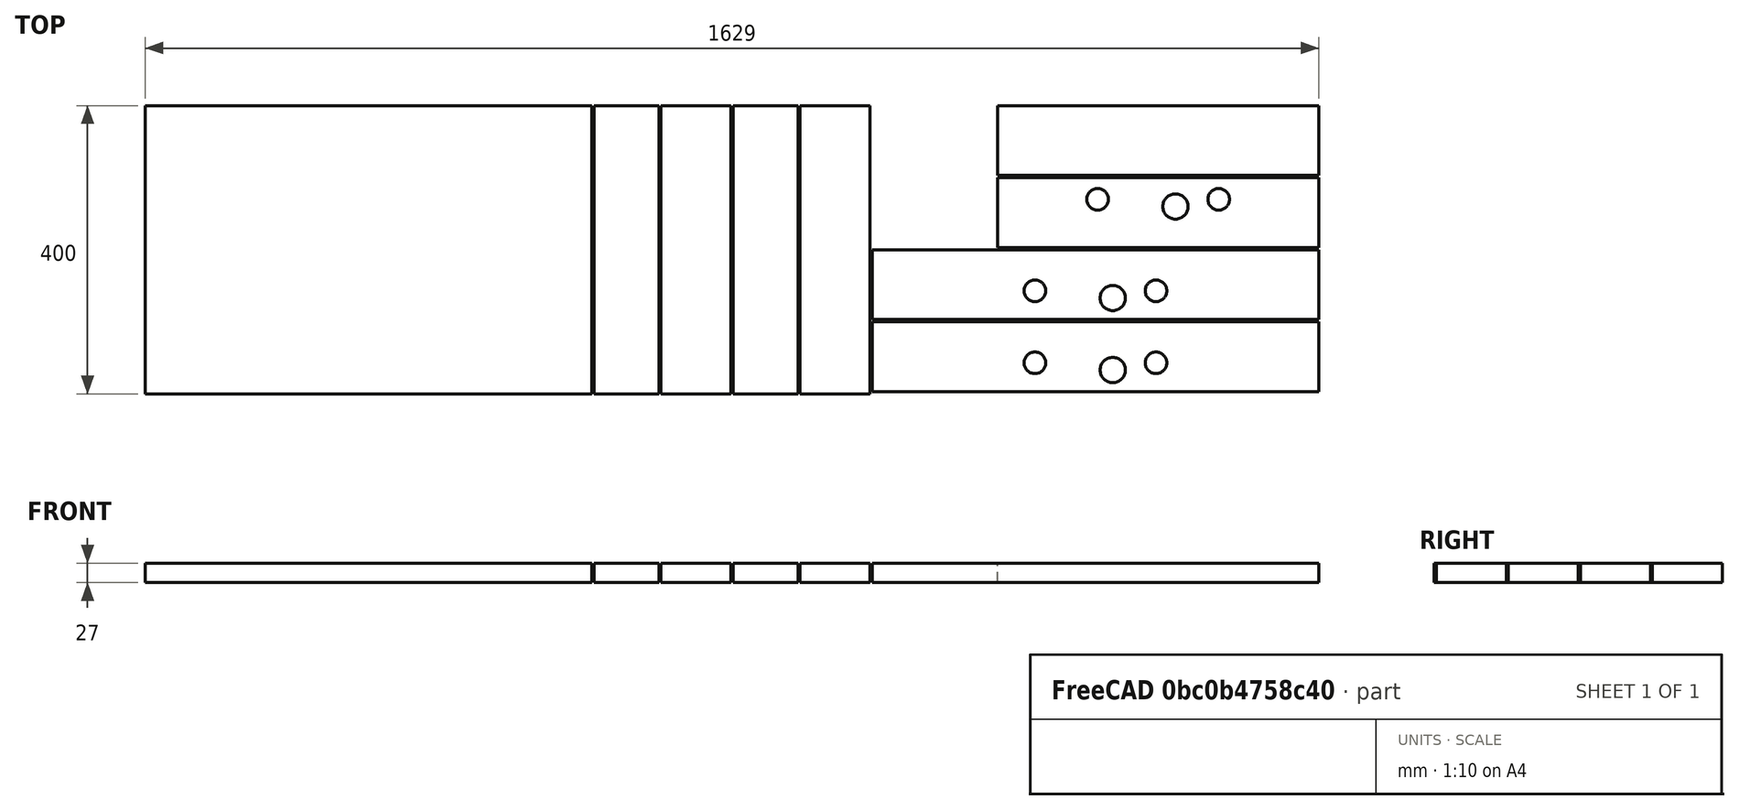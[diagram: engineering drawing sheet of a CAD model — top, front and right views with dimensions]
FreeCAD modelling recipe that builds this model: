
FCSTD DOCUMENT  (FreeCAD 0.20R25131 (Git))
Label: Zuschnitt
License: All rights reserved
LicenseURL: http://en.wikipedia.org/wiki/All_rights_reserved
objects: App::FeaturePython×70, Part::FeaturePython×41, App::Link×6, App::LinkElement×6, App::MeasureDistance×2
note: 40 computed .brp shape members not serialized (recipe doc carries the construction recipe); baked Part::Feature solids carry a one-line shape summary decoded from their .brp
EXTERNAL_REF file=Arbeitsfläche.FCStd obj=Assembly
EXTERNAL_REF file=Innen_hinten.FCStd obj=Assembly
EXTERNAL_REF file=Innen_vorne.FCStd obj=Assembly
EXTERNAL_REF file=Seitenteil.FCStd obj=Assembly
EXTERNAL_REF file=Zange.FCStd obj=Assembly
EXTERNAL_REF file=Klemmfläche.FCStd obj=Assembly

FEATURE [App::Link] Link  label="Arbeitsfläche"
  LinkedObject = -> <external Arbeitsfläche.FCStd>#Assembly
FEATURE [App::Link] Link001  label="Innen_hinten"
  LinkPlacement = pos=(1183,303,-4.4127e-12) rot=(0,0,1;0rad)
  LinkedObject = -> <external Innen_hinten.FCStd>#Assembly
  Placement = pos=(1183,303,-4.4127e-12) rot=(0,0,1;0rad)
FEATURE [App::Link] Link002  label="Innen_vorne"
  LinkPlacement = pos=(1406,203,-7.3976e-12) rot=(0,0,1;0rad)
  LinkedObject = -> <external Innen_vorne.FCStd>#Assembly
  Placement = pos=(1406,203,-7.3976e-12) rot=(0,0,1;0rad)
FEATURE [App::LinkElement] Link003_i0
  LinkPlacement = pos=(909,-4.7251e-12,-4.838e-13) rot=(0,0,1;0rad)
  LinkedObject = -> <external Seitenteil.FCStd>#Assembly
  Placement = pos=(909,-4.7251e-12,-4.838e-13) rot=(0,0,1;0rad)
FEATURE [App::LinkElement] Link003_i1
  LinkPlacement = pos=(813,400,4.313e-13) rot=(0,0,-1;3.14159rad)
  LinkedObject = -> <external Seitenteil.FCStd>#Assembly
  Placement = pos=(813,400,4.313e-13) rot=(0,0,-1;3.14159rad)
FEATURE [App::Link] Link003  label="Seitenteil"
  ElementCount = 2
  ElementList = -> [Link003_i0,Link003_i1]
  LinkedObject = -> <external Seitenteil.FCStd>#Assembly
FEATURE [App::LinkElement] Link004_i0
  LinkPlacement = pos=(1319,103,-6.2994e-12) rot=(0,0,1;0rad)
  LinkedObject = -> <external Zange.FCStd>#Assembly
  Placement = pos=(1319,103,-6.2994e-12) rot=(0,0,1;0rad)
FEATURE [App::LinkElement] Link004_i1
  LinkPlacement = pos=(1319,3,-6.3593e-12) rot=(0,0,1;0rad)
  LinkedObject = -> <external Zange.FCStd>#Assembly
  Placement = pos=(1319,3,-6.3593e-12) rot=(0,0,1;0rad)
FEATURE [App::Link] Link004  label="Zange"
  ElementCount = 2
  ElementList = -> [Link004_i0,Link004_i1]
  LinkedObject = -> <external Zange.FCStd>#Assembly
FEATURE [App::LinkElement] Link005_i0
  LinkPlacement = pos=(623,4.9e-15,2.005e-13) rot=(0,0,1;0rad)
  LinkedObject = -> <external Klemmfläche.FCStd>#Assembly
  Placement = pos=(623,4.9e-15,2.005e-13) rot=(0,0,1;0rad)
FEATURE [App::LinkElement] Link005_i1
  LinkPlacement = pos=(816,-4.5613e-12,-6.54e-14) rot=(0,0,1;0rad)
  LinkedObject = -> <external Klemmfläche.FCStd>#Assembly
  Placement = pos=(816,-4.5613e-12,-6.54e-14) rot=(0,0,1;0rad)
FEATURE [App::Link] Link005  label="Klemmfläche"
  ElementCount = 2
  ElementList = -> [Link005_i0,Link005_i1]
  LinkedObject = -> <external Klemmfläche.FCStd>#Assembly
FEATURE [Part::FeaturePython] Parts  # WARN: FeaturePython — macro-defined, semantics opaque (R4)
  Group = -> [Link,Link001,Link002,Link003,Link004,Link005]
  GroupMode = 0
FEATURE [App::MeasureDistance] Distance  label="Distance: 1629,00 mm"
  Distance = 1629
  P1 = (0,0,27)
  P2 = (1629,3,27)
FEATURE [App::MeasureDistance] Distance001  label="Distance: 1389,00 mm"
  Distance = 1389
  P1 = (0,0,0)
  P2 = (1389,3,1.605e-13)
FEATURE [Part::FeaturePython] Assembly  # WARN: FeaturePython — macro-defined, semantics opaque (R4)
  AutoRelax = true
  BuildShape = 0
  Freeze = false
  Group = -> [Constraints,Elements,Parts]
  Verbose = false
  _SolverType = 1
  _Version = 1
FEATURE [App::FeaturePython] Constraints  # WARN: FeaturePython — macro-defined, semantics opaque (R4)
  Group = -> [Constraint,Constraint001,Constraint002,Constraint003,Constraint004,Constraint005,Constraint006,Constraint007,Constraint008,Constraint009,Constraint010,Constraint011,Constraint012,Constraint013,Constraint014,Constraint015,Constraint016,Constraint017,Constraint018,Constraint019,Constraint020,Constraint021]
  _Version = 1
FEATURE [App::FeaturePython] Elements  # WARN: FeaturePython — macro-defined, semantics opaque (R4)
  Group = -> [_Element,_Element001,_Element002,_Element003,_Element004,_Element005,_Element006,_Element007,_Element008,_Element009,_Element010,_Element011,_Element012,_Element013,_Element014,_Element015,_Element016,_Element017,_Element018,_Element019,_Element020,_Element021,_Element022,_Element023,_Element024,_Element025,_Element026,_Element027,_Element028,_Element029,_Element030,_Element031,_Element032,+6 more]
FEATURE [App::FeaturePython] Constraint  label="Locked"  # WARN: FeaturePython — macro-defined, semantics opaque (R4)
  Disabled = false
  Group = -> [ElementLink]
  _ConstraintType = 0
  _Parent = -> Constraints
FEATURE [App::FeaturePython] ElementLink  label="Unten@Arbeitsfläche"  # link proxy (typed FeaturePython)
  LinkTransform = true
  LinkedObject = -> _Element
  _Parent = -> Constraint
FEATURE [Part::FeaturePython] _Element  label="Unten@Arbeitsfläche"  # link proxy (typed FeaturePython)
  Detach = false
  LinkTransform = true
  LinkedObject = -> Link [1.$Unten.]
  _Parent = -> Elements
FEATURE [Part::FeaturePython] _Element001  label="Oben@Innen_hinten"  # link proxy (typed FeaturePython)
  Detach = false
  LinkTransform = true
  LinkedObject = -> Link001 [1.$Oben.]
  _Parent = -> Elements
FEATURE [Part::FeaturePython] _Element002  label="Hinten@Arbeitsfläche"  # link proxy (typed FeaturePython)
  Detach = false
  LinkTransform = true
  LinkedObject = -> Link [1.$Hinten.]
  _Parent = -> Elements
FEATURE [App::FeaturePython] Constraint001  label="PlaneAlignment"  # WARN: FeaturePython — macro-defined, semantics opaque (R4)
  Angle = 0
  AnglePitch = 0
  AngleRoll = 0
  Cascade = false
  Disabled = false
  Group = -> [ElementLink001,ElementLink002]
  LockAngle = false
  _ConstraintType = 37
  _Parent = -> Constraints
FEATURE [App::FeaturePython] ElementLink001  label="_Element003"  # link proxy (typed FeaturePython)
  LinkTransform = true
  LinkedObject = -> _Element003
  _Parent = -> Constraint001
FEATURE [Part::FeaturePython] _Element003  # link proxy (typed FeaturePython)
  Detach = false
  LinkTransform = true
  LinkedObject = -> Link005 [0.1.$Element004.]
  _Parent = -> Elements
FEATURE [App::FeaturePython] ElementLink002  label="Oben@Arbeitsfläche"  # link proxy (typed FeaturePython)
  LinkTransform = true
  LinkedObject = -> _Element004
  _Parent = -> Constraint001
FEATURE [Part::FeaturePython] _Element004  label="Oben@Arbeitsfläche"  # link proxy (typed FeaturePython)
  Detach = false
  LinkTransform = true
  LinkedObject = -> Link [1.$Oben.]
  _Parent = -> Elements
FEATURE [App::FeaturePython] Constraint002  label="PlaneAlignment001"  # WARN: FeaturePython — macro-defined, semantics opaque (R4)
  Angle = 0
  AnglePitch = 0
  AngleRoll = 0
  Cascade = false
  Disabled = false
  Group = -> [ElementLink003,ElementLink004]
  LockAngle = false
  _ConstraintType = 37
  _Parent = -> Constraints
FEATURE [App::FeaturePython] ElementLink003  label="_Element005"  # link proxy (typed FeaturePython)
  LinkTransform = true
  LinkedObject = -> _Element005
  _Parent = -> Constraint002
FEATURE [Part::FeaturePython] _Element005  # link proxy (typed FeaturePython)
  Detach = false
  LinkTransform = true
  LinkedObject = -> Link003 [1.1.$Seite.]
  _Parent = -> Elements
FEATURE [App::FeaturePython] ElementLink004  label="_Element003"  # link proxy (typed FeaturePython)
  LinkTransform = true
  LinkedObject = -> _Element003
  _Parent = -> Constraint002
FEATURE [App::FeaturePython] Constraint003  label="PlaneAlignment002"  # WARN: FeaturePython — macro-defined, semantics opaque (R4)
  Angle = 0
  AnglePitch = 0
  AngleRoll = 0
  Cascade = false
  Disabled = false
  Group = -> [ElementLink005,ElementLink006]
  LockAngle = false
  _ConstraintType = 37
  _Parent = -> Constraints
FEATURE [App::FeaturePython] ElementLink005  label="_Element006"  # link proxy (typed FeaturePython)
  LinkTransform = true
  LinkedObject = -> _Element006
  _Parent = -> Constraint003
FEATURE [Part::FeaturePython] _Element006  # link proxy (typed FeaturePython)
  Detach = false
  LinkTransform = true
  LinkedObject = -> Link005 [1.1.$Element004.]
  _Parent = -> Elements
FEATURE [App::FeaturePython] ElementLink006  label="_Element005"  # link proxy (typed FeaturePython)
  LinkTransform = true
  LinkedObject = -> _Element005
  _Parent = -> Constraint003
FEATURE [App::FeaturePython] Constraint004  label="PlaneAlignment003"  # WARN: FeaturePython — macro-defined, semantics opaque (R4)
  Angle = 0
  AnglePitch = 0
  AngleRoll = 0
  Cascade = false
  Disabled = false
  Group = -> [ElementLink007,ElementLink008]
  LockAngle = false
  _ConstraintType = 37
  _Parent = -> Constraints
FEATURE [App::FeaturePython] ElementLink007  label="_Element007"  # link proxy (typed FeaturePython)
  LinkTransform = true
  LinkedObject = -> _Element007
  _Parent = -> Constraint004
FEATURE [Part::FeaturePython] _Element007  # link proxy (typed FeaturePython)
  Detach = false
  LinkTransform = true
  LinkedObject = -> Link003 [0.1.$Seite.]
  _Parent = -> Elements
FEATURE [App::FeaturePython] ElementLink008  label="_Element006"  # link proxy (typed FeaturePython)
  LinkTransform = true
  LinkedObject = -> _Element006
  _Parent = -> Constraint004
FEATURE [App::FeaturePython] Constraint005  label="PlaneAlignment004"  # WARN: FeaturePython — macro-defined, semantics opaque (R4)
  Angle = 0
  AnglePitch = 0
  AngleRoll = 0
  Cascade = false
  Disabled = false
  Group = -> [ElementLink009,ElementLink010]
  LockAngle = false
  Offset = 3
  _ConstraintType = 37
  _Parent = -> Constraints
FEATURE [App::FeaturePython] ElementLink009  label="_Element008"  # link proxy (typed FeaturePython)
  LinkTransform = true
  LinkedObject = -> _Element008
  _Parent = -> Constraint005
FEATURE [Part::FeaturePython] _Element008  # link proxy (typed FeaturePython)
  Detach = false
  LinkTransform = true
  LinkedObject = -> Link005 [1.1.$Rechts.]
  _Parent = -> Elements
FEATURE [App::FeaturePython] ElementLink010  label="_Element009"  # link proxy (typed FeaturePython)
  LinkTransform = true
  LinkedObject = -> _Element009
  _Parent = -> Constraint005
FEATURE [Part::FeaturePython] _Element009  # link proxy (typed FeaturePython)
  Detach = false
  LinkTransform = true
  LinkedObject = -> Link003 [0.1.$Element004.]
  _Parent = -> Elements
FEATURE [App::FeaturePython] Constraint006  label="PlaneAlignment005"  # WARN: FeaturePython — macro-defined, semantics opaque (R4)
  Angle = 0
  AnglePitch = 0
  AngleRoll = 0
  Cascade = false
  Disabled = false
  Group = -> [ElementLink011,ElementLink012]
  LockAngle = false
  Offset = -3
  _ConstraintType = 37
  _Parent = -> Constraints
FEATURE [App::FeaturePython] ElementLink011  label="_Element010"  # link proxy (typed FeaturePython)
  LinkTransform = true
  LinkedObject = -> _Element010
  _Parent = -> Constraint006
FEATURE [Part::FeaturePython] _Element010  # link proxy (typed FeaturePython)
  Detach = false
  LinkTransform = true
  LinkedObject = -> Link005 [1.1.$Links.]
  _Parent = -> Elements
FEATURE [App::FeaturePython] ElementLink012  label="_Element011"  # link proxy (typed FeaturePython)
  LinkTransform = true
  LinkedObject = -> _Element011
  _Parent = -> Constraint006
FEATURE [Part::FeaturePython] _Element011  # link proxy (typed FeaturePython)
  Detach = false
  LinkTransform = true
  LinkedObject = -> Link003 [1.1.$Element004.]
  _Parent = -> Elements
FEATURE [App::FeaturePython] Constraint007  label="PlaneAlignment006"  # WARN: FeaturePython — macro-defined, semantics opaque (R4)
  Angle = 0
  AnglePitch = 0
  AngleRoll = 0
  Cascade = false
  Disabled = false
  Group = -> [ElementLink013,ElementLink014]
  LockAngle = false
  Offset = 3
  _ConstraintType = 37
  _Parent = -> Constraints
FEATURE [App::FeaturePython] ElementLink013  label="_Element012"  # link proxy (typed FeaturePython)
  LinkTransform = true
  LinkedObject = -> _Element012
  _Parent = -> Constraint007
FEATURE [Part::FeaturePython] _Element012  # link proxy (typed FeaturePython)
  Detach = false
  LinkTransform = true
  LinkedObject = -> Link005 [0.1.$Rechts.]
  _Parent = -> Elements
FEATURE [App::FeaturePython] ElementLink014  label="_Element013"  # link proxy (typed FeaturePython)
  LinkTransform = true
  LinkedObject = -> _Element013
  _Parent = -> Constraint007
FEATURE [Part::FeaturePython] _Element013  # link proxy (typed FeaturePython)
  Detach = false
  LinkTransform = true
  LinkedObject = -> Link003 [1.1.$Oben.]
  _Parent = -> Elements
FEATURE [App::FeaturePython] Constraint008  label="PlaneAlignment007"  # WARN: FeaturePython — macro-defined, semantics opaque (R4)
  Angle = 0
  AnglePitch = 0
  AngleRoll = 0
  Cascade = false
  Disabled = false
  Group = -> [ElementLink015,ElementLink016]
  LockAngle = false
  Offset = -3
  _ConstraintType = 37
  _Parent = -> Constraints
FEATURE [App::FeaturePython] ElementLink015  label="_Element014"  # link proxy (typed FeaturePython)
  LinkTransform = true
  LinkedObject = -> _Element014
  _Parent = -> Constraint008
FEATURE [Part::FeaturePython] _Element014  # link proxy (typed FeaturePython)
  Detach = false
  LinkTransform = true
  LinkedObject = -> Link005 [0.1.$Links.]
  _Parent = -> Elements
FEATURE [App::FeaturePython] ElementLink016  label="Rechts@Arbeitsfläche"  # link proxy (typed FeaturePython)
  LinkTransform = true
  LinkedObject = -> _Element015
  _Parent = -> Constraint008
FEATURE [Part::FeaturePython] _Element015  label="Rechts@Arbeitsfläche"  # link proxy (typed FeaturePython)
  Detach = false
  LinkTransform = true
  LinkedObject = -> Link [1.$Rechts.]
  _Parent = -> Elements
FEATURE [App::FeaturePython] Constraint009  label="PlaneAlignment008"  # WARN: FeaturePython — macro-defined, semantics opaque (R4)
  Angle = 0
  AnglePitch = 0
  AngleRoll = 0
  Cascade = false
  Disabled = false
  Group = -> [ElementLink017,ElementLink018]
  LockAngle = false
  _ConstraintType = 37
  _Parent = -> Constraints
FEATURE [App::FeaturePython] ElementLink017  label="Vorne@Arbeitsfläche"  # link proxy (typed FeaturePython)
  LinkTransform = true
  LinkedObject = -> _Element016
  _Parent = -> Constraint009
FEATURE [Part::FeaturePython] _Element016  label="Vorne@Arbeitsfläche"  # link proxy (typed FeaturePython)
  Detach = false
  LinkTransform = true
  LinkedObject = -> Link [1.$Vorne.]
  _Parent = -> Elements
FEATURE [App::FeaturePython] ElementLink018  label="_Element017"  # link proxy (typed FeaturePython)
  LinkTransform = true
  LinkedObject = -> _Element017
  _Parent = -> Constraint009
FEATURE [Part::FeaturePython] _Element017  # link proxy (typed FeaturePython)
  Detach = false
  LinkTransform = true
  LinkedObject = -> Link005 [0.1.$Vorne.]
  _Parent = -> Elements
FEATURE [App::FeaturePython] Constraint010  label="PlaneAlignment009"  # WARN: FeaturePython — macro-defined, semantics opaque (R4)
  Angle = 0
  AnglePitch = 0
  AngleRoll = 0
  Cascade = false
  Disabled = false
  Group = -> [ElementLink019,ElementLink020]
  LockAngle = false
  _ConstraintType = 37
  _Parent = -> Constraints
FEATURE [App::FeaturePython] ElementLink019  label="_Element017"  # link proxy (typed FeaturePython)
  LinkTransform = true
  LinkedObject = -> _Element017
  _Parent = -> Constraint010
FEATURE [App::FeaturePython] ElementLink020  label="_Element018"  # link proxy (typed FeaturePython)
  LinkTransform = true
  LinkedObject = -> _Element018
  _Parent = -> Constraint010
FEATURE [Part::FeaturePython] _Element018  # link proxy (typed FeaturePython)
  Detach = false
  LinkTransform = true
  LinkedObject = -> Link003 [1.1.$Element005.]
  _Parent = -> Elements
FEATURE [App::FeaturePython] Constraint011  label="PlaneAlignment010"  # WARN: FeaturePython — macro-defined, semantics opaque (R4)
  Angle = 0
  AnglePitch = 0
  AngleRoll = 0
  Cascade = false
  Disabled = false
  Group = -> [ElementLink021,ElementLink022,ElementLink023]
  LockAngle = false
  _ConstraintType = 37
  _Parent = -> Constraints
FEATURE [App::FeaturePython] ElementLink021  label="_Element019"  # link proxy (typed FeaturePython)
  LinkTransform = true
  LinkedObject = -> _Element019
  _Parent = -> Constraint011
FEATURE [Part::FeaturePython] _Element019  # link proxy (typed FeaturePython)
  Detach = false
  LinkTransform = true
  LinkedObject = -> Link005 [1.1.$Vorne.]
  _Parent = -> Elements
FEATURE [App::FeaturePython] ElementLink022  label="_Element018"  # link proxy (typed FeaturePython)
  LinkTransform = true
  LinkedObject = -> _Element018
  _Parent = -> Constraint011
FEATURE [App::FeaturePython] ElementLink023  label="_Element020"  # link proxy (typed FeaturePython)
  LinkTransform = true
  LinkedObject = -> _Element020
  _Parent = -> Constraint011
FEATURE [Part::FeaturePython] _Element020  # link proxy (typed FeaturePython)
  Detach = false
  LinkTransform = true
  LinkedObject = -> Link003 [0.1.$Vorne.]
  _Parent = -> Elements
FEATURE [App::FeaturePython] Constraint012  label="PlaneAlignment011"  # WARN: FeaturePython — macro-defined, semantics opaque (R4)
  Angle = 0
  AnglePitch = 0
  AngleRoll = 0
  Cascade = false
  Disabled = false
  Group = -> [ElementLink024,ElementLink025]
  LockAngle = false
  _ConstraintType = 37
  _Parent = -> Constraints
FEATURE [App::FeaturePython] ElementLink024  label="Vorne@Innen_vorne"  # link proxy (typed FeaturePython)
  LinkTransform = true
  LinkedObject = -> _Element021
  _Parent = -> Constraint012
FEATURE [Part::FeaturePython] _Element021  label="Vorne@Innen_vorne"  # link proxy (typed FeaturePython)
  Detach = false
  LinkTransform = true
  LinkedObject = -> Link002 [1.$Vorne.]
  _Parent = -> Elements
FEATURE [App::FeaturePython] ElementLink025  label="_Element022"  # link proxy (typed FeaturePython)
  LinkTransform = true
  LinkedObject = -> _Element022
  _Parent = -> Constraint012
FEATURE [Part::FeaturePython] _Element022  # link proxy (typed FeaturePython)
  Detach = false
  LinkTransform = true
  LinkedObject = -> Link001 [1.$Element003.]
  _Parent = -> Elements
FEATURE [App::FeaturePython] Constraint013  label="PlaneAlignment012"  # WARN: FeaturePython — macro-defined, semantics opaque (R4)
  Angle = 0
  AnglePitch = 0
  AngleRoll = 0
  Cascade = false
  Disabled = false
  Group = -> [ElementLink026,ElementLink027]
  LockAngle = false
  _ConstraintType = 37
  _Parent = -> Constraints
FEATURE [App::FeaturePython] ElementLink026  label="_Element023"  # link proxy (typed FeaturePython)
  LinkTransform = true
  LinkedObject = -> _Element023
  _Parent = -> Constraint013
FEATURE [Part::FeaturePython] _Element023  # link proxy (typed FeaturePython)
  Detach = false
  LinkTransform = true
  LinkedObject = -> Link002 [1.$Element005.]
  _Parent = -> Elements
FEATURE [App::FeaturePython] ElementLink027  label="_Element024"  # link proxy (typed FeaturePython)
  LinkTransform = true
  LinkedObject = -> _Element024
  _Parent = -> Constraint013
FEATURE [Part::FeaturePython] _Element024  # link proxy (typed FeaturePython)
  Detach = false
  LinkTransform = true
  LinkedObject = -> Link001 [1.$Element004.]
  _Parent = -> Elements
FEATURE [App::FeaturePython] Constraint014  label="PlaneAlignment013"  # WARN: FeaturePython — macro-defined, semantics opaque (R4)
  Angle = 0
  AnglePitch = 0
  AngleRoll = 0
  Cascade = false
  Disabled = false
  Group = -> [ElementLink028,ElementLink029]
  LockAngle = false
  Offset = -3
  _ConstraintType = 37
  _Parent = -> Constraints
FEATURE [App::FeaturePython] ElementLink028  label="_Element025"  # link proxy (typed FeaturePython)
  LinkTransform = true
  LinkedObject = -> _Element025
  _Parent = -> Constraint014
FEATURE [Part::FeaturePython] _Element025  # link proxy (typed FeaturePython)
  Detach = false
  LinkTransform = true
  LinkedObject = -> Link001 [1.$Element005.]
  _Parent = -> Elements
FEATURE [App::FeaturePython] ElementLink029  label="Oben@Innen_vorne"  # link proxy (typed FeaturePython)
  LinkTransform = true
  LinkedObject = -> _Element026
  _Parent = -> Constraint014
FEATURE [Part::FeaturePython] _Element026  label="Oben@Innen_vorne"  # link proxy (typed FeaturePython)
  Detach = false
  LinkTransform = true
  LinkedObject = -> Link002 [1.$Oben.]
  _Parent = -> Elements
FEATURE [App::FeaturePython] Constraint015  label="PlaneAlignment014"  # WARN: FeaturePython — macro-defined, semantics opaque (R4)
  Angle = 0
  AnglePitch = 0
  AngleRoll = 0
  Cascade = false
  Disabled = false
  Group = -> [ElementLink030,ElementLink031]
  LockAngle = false
  _ConstraintType = 37
  _Parent = -> Constraints
FEATURE [App::FeaturePython] ElementLink030  label="Oben@Innen_hinten"  # link proxy (typed FeaturePython)
  LinkTransform = true
  LinkedObject = -> _Element001
  _Parent = -> Constraint015
FEATURE [App::FeaturePython] ElementLink031  label="_Element027"  # link proxy (typed FeaturePython)
  LinkTransform = true
  LinkedObject = -> _Element027
  _Parent = -> Constraint015
FEATURE [Part::FeaturePython] _Element027  # link proxy (typed FeaturePython)
  Detach = false
  LinkTransform = true
  LinkedObject = -> Link003 [0.1.$Element005.]
  _Parent = -> Elements
FEATURE [App::FeaturePython] Constraint016  label="PlaneAlignment015"  # WARN: FeaturePython — macro-defined, semantics opaque (R4)
  Angle = 0
  AnglePitch = 0
  AngleRoll = 0
  Cascade = false
  Disabled = false
  Group = -> [ElementLink032,ElementLink033]
  LockAngle = false
  _ConstraintType = 37
  _Parent = -> Constraints
FEATURE [App::FeaturePython] ElementLink032  label="_Element022"  # link proxy (typed FeaturePython)
  LinkTransform = true
  LinkedObject = -> _Element022
  _Parent = -> Constraint016
FEATURE [App::FeaturePython] ElementLink033  label="_Element007"  # link proxy (typed FeaturePython)
  LinkTransform = true
  LinkedObject = -> _Element007
  _Parent = -> Constraint016
FEATURE [Part::FeaturePython] _Element028  # link proxy (typed FeaturePython)
  Detach = false
  LinkTransform = true
  LinkedObject = -> Link004 [1.1.$Hinten.]
  _Parent = -> Elements
FEATURE [App::FeaturePython] Constraint017  label="PlaneAlignment016"  # WARN: FeaturePython — macro-defined, semantics opaque (R4)
  Angle = 0
  AnglePitch = 0
  AngleRoll = 0
  Cascade = false
  Disabled = false
  Group = -> [ElementLink034,ElementLink035,ElementLink036]
  LockAngle = false
  _ConstraintType = 37
  _Parent = -> Constraints
FEATURE [App::FeaturePython] ElementLink034  label="_Element029"  # link proxy (typed FeaturePython)
  LinkTransform = true
  LinkedObject = -> _Element029
  _Parent = -> Constraint017
FEATURE [Part::FeaturePython] _Element029  # link proxy (typed FeaturePython)
  Detach = false
  LinkTransform = true
  LinkedObject = -> Link004 [0.1.$Element005.]
  _Parent = -> Elements
FEATURE [App::FeaturePython] ElementLink035  label="_Element030"  # link proxy (typed FeaturePython)
  LinkTransform = true
  LinkedObject = -> _Element030
  _Parent = -> Constraint017
FEATURE [Part::FeaturePython] _Element030  # link proxy (typed FeaturePython)
  Detach = false
  LinkTransform = true
  LinkedObject = -> Link004 [1.1.$Element005.]
  _Parent = -> Elements
FEATURE [App::FeaturePython] ElementLink036  label="_Element023"  # link proxy (typed FeaturePython)
  LinkTransform = true
  LinkedObject = -> _Element023
  _Parent = -> Constraint017
FEATURE [App::FeaturePython] Constraint018  label="PlaneAlignment017"  # WARN: FeaturePython — macro-defined, semantics opaque (R4)
  Angle = 0
  AnglePitch = 0
  AngleRoll = 0
  Cascade = false
  Disabled = false
  Group = -> [ElementLink037,ElementLink038,ElementLink039]
  LockAngle = false
  _ConstraintType = 37
  _Parent = -> Constraints
FEATURE [App::FeaturePython] ElementLink037  label="_Element031"  # link proxy (typed FeaturePython)
  LinkTransform = true
  LinkedObject = -> _Element031
  _Parent = -> Constraint018
FEATURE [Part::FeaturePython] _Element031  # link proxy (typed FeaturePython)
  Detach = false
  LinkTransform = true
  LinkedObject = -> Link004 [1.1.$Vorne.]
  _Parent = -> Elements
FEATURE [App::FeaturePython] ElementLink038  label="_Element032"  # link proxy (typed FeaturePython)
  LinkTransform = true
  LinkedObject = -> _Element032
  _Parent = -> Constraint018
FEATURE [Part::FeaturePython] _Element032  # link proxy (typed FeaturePython)
  Detach = false
  LinkTransform = true
  LinkedObject = -> Link004 [0.1.$Vorne.]
  _Parent = -> Elements
FEATURE [App::FeaturePython] ElementLink039  label="Vorne@Innen_vorne"  # link proxy (typed FeaturePython)
  LinkTransform = true
  LinkedObject = -> _Element021
  _Parent = -> Constraint018
FEATURE [App::FeaturePython] Constraint019  label="PlaneAlignment018"  # WARN: FeaturePython — macro-defined, semantics opaque (R4)
  Angle = 0
  AnglePitch = 0
  AngleRoll = 0
  Cascade = false
  Disabled = false
  Group = -> [ElementLink040,ElementLink041]
  LockAngle = false
  Offset = 3
  _ConstraintType = 37
  _Parent = -> Constraints
FEATURE [App::FeaturePython] ElementLink040  label="_Element033"  # link proxy (typed FeaturePython)
  LinkTransform = true
  LinkedObject = -> _Element033
  _Parent = -> Constraint019
FEATURE [Part::FeaturePython] _Element033  # link proxy (typed FeaturePython)
  Detach = false
  LinkTransform = true
  LinkedObject = -> Link004 [0.1.$Oben.]
  _Parent = -> Elements
FEATURE [App::FeaturePython] ElementLink041  label="_Element034"  # link proxy (typed FeaturePython)
  LinkTransform = true
  LinkedObject = -> _Element034
  _Parent = -> Constraint019
FEATURE [Part::FeaturePython] _Element034  # link proxy (typed FeaturePython)
  Detach = false
  LinkTransform = true
  LinkedObject = -> Link002 [1.$Element006.]
  _Parent = -> Elements
FEATURE [App::FeaturePython] Constraint020  label="PlaneAlignment019"  # WARN: FeaturePython — macro-defined, semantics opaque (R4)
  Angle = 0
  AnglePitch = 0
  AngleRoll = 0
  Cascade = false
  Disabled = false
  Group = -> [ElementLink042,ElementLink043]
  LockAngle = false
  Offset = -3
  _ConstraintType = 37
  _Parent = -> Constraints
FEATURE [App::FeaturePython] ElementLink042  label="_Element035"  # link proxy (typed FeaturePython)
  LinkTransform = true
  LinkedObject = -> _Element035
  _Parent = -> Constraint020
FEATURE [Part::FeaturePython] _Element035  # link proxy (typed FeaturePython)
  Detach = false
  LinkTransform = true
  LinkedObject = -> Link004 [0.1.$Element006.]
  _Parent = -> Elements
FEATURE [App::FeaturePython] ElementLink043  label="_Element036"  # link proxy (typed FeaturePython)
  LinkTransform = true
  LinkedObject = -> _Element036
  _Parent = -> Constraint020
FEATURE [Part::FeaturePython] _Element036  # link proxy (typed FeaturePython)
  Detach = false
  LinkTransform = true
  LinkedObject = -> Link004 [1.1.$Oben.]
  _Parent = -> Elements
FEATURE [App::FeaturePython] Constraint021  label="PlaneAlignment020"  # WARN: FeaturePython — macro-defined, semantics opaque (R4)
  Angle = 0
  AnglePitch = 0
  AngleRoll = 0
  Cascade = false
  Disabled = false
  Group = -> [ElementLink044,ElementLink045]
  LockAngle = false
  Offset = -3
  _ConstraintType = 37
  _Parent = -> Constraints
FEATURE [App::FeaturePython] ElementLink044  label="_Element037"  # link proxy (typed FeaturePython)
  LinkTransform = true
  LinkedObject = -> _Element037
  _Parent = -> Constraint021
FEATURE [Part::FeaturePython] _Element037  # link proxy (typed FeaturePython)
  Detach = false
  LinkTransform = true
  LinkedObject = -> Link004 [0.1.$Element007.]
  _Parent = -> Elements
FEATURE [App::FeaturePython] ElementLink045  label="_Element038"  # link proxy (typed FeaturePython)
  LinkTransform = true
  LinkedObject = -> _Element038
  _Parent = -> Constraint021
FEATURE [Part::FeaturePython] _Element038  # link proxy (typed FeaturePython)
  Detach = false
  LinkTransform = true
  LinkedObject = -> Link003 [0.1.$Oben.]
  _Parent = -> Elements

RESOLVED EXTERNAL PARTS (link-assembly join: the EXTERNAL_REF files above that resolve inside this repo's crawl, each included once):
---- part Arbeitsfläche.FCStd = doc fcstd_90bbc381280e ----
FCSTD DOCUMENT  (FreeCAD 0.20R25131 (Git))
Label: Arbeitsfläche
License: All rights reserved
LicenseURL: http://en.wikipedia.org/wiki/All_rights_reserved
objects: Part::FeaturePython×8, App::FeaturePython×2, Part::Box×1, Part::Cylinder×1, Part::Cut×1
note: 10 computed .brp shape members not serialized (recipe doc carries the construction recipe); baked Part::Feature solids carry a one-line shape summary decoded from their .brp
EXTERNAL_REF file=Grunddaten.FCStd obj=Spreadsheet

FEATURE [Part::Box] Box  label="Cube"
  AttacherType = Attacher::AttachEngine3D
  Height = 27
  Length = 620
  Width = 400
  expr: Length = <<Grunddaten>>#Spreadsheet.Arbeitsflaeche + 2 * <<Grunddaten>>#Spreadsheet.Ueberstand
  expr: Width = <<Grunddaten>>#Spreadsheet.Plattenbreite
  expr: Height = <<Grunddaten>>#Spreadsheet.Plattendicke
FEATURE [App::FeaturePython] Constraints  # WARN: FeaturePython — macro-defined, semantics opaque (R4)
  _Version = 1
FEATURE [Part::Cylinder] Cylinder  label="Schraubzwinge_oben"
  Angle = 360
  AttacherType = Attacher::AttachEngine3D
  FirstAngle = 0
  Height = 30
  Placement = pos=(485,60,0) rot=(0,0,1;0rad)
  Radius = 25
  SecondAngle = 0
  expr: .Placement.Base.x = Grunddaten#Spreadsheet.Arbeitsflaeche + Grunddaten#Spreadsheet.Ueberstand - 75mm
FEATURE [Part::Cut] Cut
  Base = -> Box
  Tool = -> Cylinder
FEATURE [Part::FeaturePython] Parts  # WARN: FeaturePython — macro-defined, semantics opaque (R4)
  Group = -> [Box,Cylinder,Cut]
  GroupMode = 0
FEATURE [Part::FeaturePython] Assembly  label="Arbeitsfläche"  # WARN: FeaturePython — macro-defined, semantics opaque (R4)
  AutoRelax = true
  BuildShape = 0
  Freeze = false
  Group = -> [Constraints,Elements,Parts]
  Verbose = false
  _SolverType = 1
  _Version = 1
FEATURE [App::FeaturePython] Elements  # WARN: FeaturePython — macro-defined, semantics opaque (R4)
  Group = -> [Element,Element001,Element002,Element003,Element004,Element005]
FEATURE [Part::FeaturePython] Element  label="Unten"  # link proxy (typed FeaturePython)
  Detach = false
  LinkTransform = true
  LinkedObject = -> Box [Face5]
  _Parent = -> Elements
FEATURE [Part::FeaturePython] Element001  label="Vorne"  # link proxy (typed FeaturePython)
  Detach = false
  LinkTransform = true
  LinkedObject = -> Box [Face3]
  _Parent = -> Elements
FEATURE [Part::FeaturePython] Element002  label="Hinten"  # link proxy (typed FeaturePython)
  Detach = false
  LinkTransform = true
  LinkedObject = -> Box [Face4]
  _Parent = -> Elements
FEATURE [Part::FeaturePython] Element003  label="Rechts"  # link proxy (typed FeaturePython)
  Detach = false
  LinkTransform = true
  LinkedObject = -> Box [Face2]
  _Parent = -> Elements
FEATURE [Part::FeaturePython] Element004  label="Links"  # link proxy (typed FeaturePython)
  Detach = false
  LinkTransform = true
  LinkedObject = -> Box [Face1]
  _Parent = -> Elements
FEATURE [Part::FeaturePython] Element005  label="Oben"  # link proxy (typed FeaturePython)
  Detach = false
  LinkTransform = true
  LinkedObject = -> Box [Face6]
  _Parent = -> Elements
---- part Innen_hinten.FCStd = doc fcstd_743176cbf1e2 ----
FCSTD DOCUMENT  (FreeCAD 0.20R25131 (Git))
Label: Innen_hinten
License: All rights reserved
LicenseURL: http://en.wikipedia.org/wiki/All_rights_reserved
objects: Part::FeaturePython×8, App::FeaturePython×2, Part::Box×1
note: 8 computed .brp shape members not serialized (recipe doc carries the construction recipe); baked Part::Feature solids carry a one-line shape summary decoded from their .brp
EXTERNAL_REF file=Grunddaten.FCStd obj=Spreadsheet

FEATURE [Part::Box] Box  label="Cube"
  AttacherType = Attacher::AttachEngine3D
  Height = 27
  Length = 446
  Width = 97
  expr: Length = <<Grunddaten>>#Spreadsheet.Innenmass
  expr: Width = <<Grunddaten>>#Spreadsheet.Hoehe
  expr: Height = <<Grunddaten>>#Spreadsheet.Plattendicke
FEATURE [App::FeaturePython] Constraints  # WARN: FeaturePython — macro-defined, semantics opaque (R4)
  _Version = 1
FEATURE [Part::FeaturePython] Parts  # WARN: FeaturePython — macro-defined, semantics opaque (R4)
  Group = -> [Box]
  GroupMode = 0
FEATURE [Part::FeaturePython] Assembly  label="Innen_hinten"  # WARN: FeaturePython — macro-defined, semantics opaque (R4)
  AutoRelax = true
  BuildShape = 0
  Freeze = false
  Group = -> [Constraints,Elements,Parts]
  Verbose = false
  _SolverType = 1
  _Version = 1
FEATURE [App::FeaturePython] Elements  # WARN: FeaturePython — macro-defined, semantics opaque (R4)
  Group = -> [Element,Element001,Element002,Element003,Element004,Element005]
FEATURE [Part::FeaturePython] Element  label="Oben"  # link proxy (typed FeaturePython)
  Detach = false
  LinkTransform = true
  LinkedObject = -> Box [Face4]
  _Parent = -> Elements
FEATURE [Part::FeaturePython] Element001  label="Hinten"  # link proxy (typed FeaturePython)
  Detach = false
  LinkTransform = true
  LinkedObject = -> Box [Face5]
  _Parent = -> Elements
FEATURE [Part::FeaturePython] Element002  # link proxy (typed FeaturePython)
  Detach = false
  LinkTransform = true
  LinkedObject = -> Box [Face1]
  _Parent = -> Elements
FEATURE [Part::FeaturePython] Element003  # link proxy (typed FeaturePython)
  Detach = false
  LinkTransform = true
  LinkedObject = -> Box [Face6]
  _Parent = -> Elements
FEATURE [Part::FeaturePython] Element004  # link proxy (typed FeaturePython)
  Detach = false
  LinkTransform = true
  LinkedObject = -> Box [Face2]
  _Parent = -> Elements
FEATURE [Part::FeaturePython] Element005  # link proxy (typed FeaturePython)
  Detach = false
  LinkTransform = true
  LinkedObject = -> Box [Face3]
  _Parent = -> Elements
---- part Innen_vorne.FCStd = doc fcstd_2986dde7ab49 ----
FCSTD DOCUMENT  (FreeCAD 0.20R25131 (Git))
Label: Innen_vorne
License: All rights reserved
LicenseURL: http://en.wikipedia.org/wiki/All_rights_reserved
objects: Part::FeaturePython×9, Part::Cylinder×3, App::FeaturePython×2, Part::Box×1, Part::MultiFuse×1, Part::Cut×1
note: 14 computed .brp shape members not serialized (recipe doc carries the construction recipe); baked Part::Feature solids carry a one-line shape summary decoded from their .brp
EXTERNAL_REF file=Grunddaten.FCStd obj=Spreadsheet

FEATURE [Part::Box] Box  label="Cube"
  AttacherType = Attacher::AttachEngine3D
  Height = 27
  Length = 446
  Placement = pos=(-223,0,0) rot=(0,0,1;0rad)
  Width = 97
  expr: .Placement.Base.x = -Length / 2
  expr: Height = <<Grunddaten>>#Spreadsheet.Plattendicke
  expr: Width = <<Grunddaten>>#Spreadsheet.Hoehe
  expr: Length = <<Grunddaten>>#Spreadsheet.Innenmass
FEATURE [Part::Cylinder] Cylinder  label="Führung_rechts"
  Angle = 360
  AttacherType = Attacher::AttachEngine3D
  FirstAngle = 0
  Height = 30
  Placement = pos=(84,67,0) rot=(0,0,1;0rad)
  Radius = 15
  SecondAngle = 0
  expr: .Placement.Base.x = Grunddaten#Spreadsheet.Spindel_Links
  expr: .Placement.Base.y = Grunddaten#Spreadsheet.Hoehe - Grunddaten#Spreadsheet.Spindel_Hoehe
FEATURE [Part::Cylinder] Cylinder001  label="Führung_links"
  Angle = 360
  AttacherType = Attacher::AttachEngine3D
  FirstAngle = 0
  Height = 30
  Placement = pos=(-84,67,0) rot=(0,0,1;0rad)
  Radius = 15
  SecondAngle = 0
  expr: .Placement.Base.x = -Grunddaten#Spreadsheet.Spindel_Links
  expr: .Placement.Base.y = Grunddaten#Spreadsheet.Hoehe - Grunddaten#Spreadsheet.Spindel_Hoehe
FEATURE [Part::Cylinder] Cylinder002  label="Spindel"
  Angle = 360
  AttacherType = Attacher::AttachEngine3D
  FirstAngle = 0
  Height = 30
  Placement = pos=(24,57,0) rot=(0,0,1;0rad)
  Radius = 17.5
  SecondAngle = 0
  expr: .Placement.Base.y = Grunddaten#Spreadsheet.Hoehe - Grunddaten#Spreadsheet.Spindel_Antrieb_Hoehe
  expr: .Placement.Base.x = Grunddaten#Spreadsheet.Spindel_Antrieb
FEATURE [App::FeaturePython] Constraints  # WARN: FeaturePython — macro-defined, semantics opaque (R4)
  _Version = 1
FEATURE [Part::MultiFuse] Fusion
  Shapes = -> [Cylinder,Cylinder001,Cylinder002]
FEATURE [Part::Cut] Cut
  Base = -> Box
  Tool = -> Fusion
FEATURE [Part::FeaturePython] Parts  # WARN: FeaturePython — macro-defined, semantics opaque (R4)
  Group = -> [Box,Cylinder,Cylinder001,Cylinder002,Fusion,Cut]
  GroupMode = 0
FEATURE [Part::FeaturePython] Assembly  label="Innen_vorne"  # WARN: FeaturePython — macro-defined, semantics opaque (R4)
  AutoRelax = true
  BuildShape = 0
  Freeze = false
  Group = -> [Constraints,Elements,Parts]
  Verbose = false
  _SolverType = 1
  _Version = 1
FEATURE [App::FeaturePython] Elements  # WARN: FeaturePython — macro-defined, semantics opaque (R4)
  Group = -> [Element,Element001,Element002,Element003,Element004,Element005,Element006]
FEATURE [Part::FeaturePython] Element  label="Vorne"  # link proxy (typed FeaturePython)
  Detach = false
  LinkTransform = true
  LinkedObject = -> Cut [Face3]
  _Parent = -> Elements
FEATURE [Part::FeaturePython] Element001  label="Oben"  # link proxy (typed FeaturePython)
  Detach = false
  LinkTransform = true
  LinkedObject = -> Cut [Face4]
  _Parent = -> Elements
FEATURE [Part::FeaturePython] Element002  label="Spindel"  # link proxy (typed FeaturePython)
  Detach = false
  LinkTransform = true
  LinkedObject = -> Cut [Face7]
  _Parent = -> Elements
FEATURE [Part::FeaturePython] Element003  # link proxy (typed FeaturePython)
  Detach = false
  LinkTransform = true
  LinkedObject = -> Cut [Edge10]
  _Parent = -> Elements
FEATURE [Part::FeaturePython] Element004  # link proxy (typed FeaturePython)
  Detach = false
  LinkTransform = true
  LinkedObject = -> Cut [Face1]
  _Parent = -> Elements
FEATURE [Part::FeaturePython] Element005  # link proxy (typed FeaturePython)
  Detach = false
  LinkTransform = true
  LinkedObject = -> Cut [Face6]
  _Parent = -> Elements
FEATURE [Part::FeaturePython] Element006  # link proxy (typed FeaturePython)
  Detach = false
  LinkTransform = true
  LinkedObject = -> Cut [Face2]
  _Parent = -> Elements
---- part Klemmfläche.FCStd = doc fcstd_d60b58048bda ----
FCSTD DOCUMENT  (FreeCAD 0.20R25131 (Git))
Label: Klemmfläche
License: All rights reserved
LicenseURL: http://en.wikipedia.org/wiki/All_rights_reserved
objects: Part::FeaturePython×7, App::FeaturePython×2, Part::Box×1
note: 7 computed .brp shape members not serialized (recipe doc carries the construction recipe); baked Part::Feature solids carry a one-line shape summary decoded from their .brp
EXTERNAL_REF file=Grunddaten.FCStd obj=Spreadsheet

FEATURE [Part::Box] Box  label="Cube"
  AttacherType = Attacher::AttachEngine3D
  Height = 27
  Length = 90
  Width = 400
  expr: Length = <<Grunddaten>>#Spreadsheet.Klemmflaeche
  expr: Width = <<Grunddaten>>#Spreadsheet.Plattenbreite
  expr: Height = <<Grunddaten>>#Spreadsheet.Plattendicke
FEATURE [App::FeaturePython] Constraints  # WARN: FeaturePython — macro-defined, semantics opaque (R4)
  _Version = 1
FEATURE [Part::FeaturePython] Parts  # WARN: FeaturePython — macro-defined, semantics opaque (R4)
  Group = -> [Box]
  GroupMode = 0
FEATURE [Part::FeaturePython] Assembly  label="Klemmfläche"  # WARN: FeaturePython — macro-defined, semantics opaque (R4)
  AutoRelax = true
  BuildShape = 0
  Freeze = false
  Group = -> [Constraints,Elements,Parts]
  Verbose = false
  _SolverType = 1
  _Version = 1
FEATURE [App::FeaturePython] Elements  # WARN: FeaturePython — macro-defined, semantics opaque (R4)
  Group = -> [Element,Element001,Element002,Element003,Element004]
FEATURE [Part::FeaturePython] Element  label="Vorne"  # link proxy (typed FeaturePython)
  Detach = false
  LinkTransform = true
  LinkedObject = -> Box [Face3]
  _Parent = -> Elements
FEATURE [Part::FeaturePython] Element001  label="Unten"  # link proxy (typed FeaturePython)
  Detach = false
  LinkTransform = true
  LinkedObject = -> Box [Face5]
  _Parent = -> Elements
FEATURE [Part::FeaturePython] Element002  label="Rechts"  # link proxy (typed FeaturePython)
  Detach = false
  LinkTransform = true
  LinkedObject = -> Box [Face2]
  _Parent = -> Elements
FEATURE [Part::FeaturePython] Element003  label="Links"  # link proxy (typed FeaturePython)
  Detach = false
  LinkTransform = true
  LinkedObject = -> Box [Face1]
  _Parent = -> Elements
FEATURE [Part::FeaturePython] Element004  # link proxy (typed FeaturePython)
  Detach = false
  LinkTransform = true
  LinkedObject = -> Box [Face6]
  _Parent = -> Elements
---- part Seitenteil.FCStd = doc fcstd_1cb6ae5e1e0b ----
FCSTD DOCUMENT  (FreeCAD 0.20R25131 (Git))
Label: Seitenteil
License: All rights reserved
LicenseURL: http://en.wikipedia.org/wiki/All_rights_reserved
objects: Part::FeaturePython×8, Part::Box×2, App::FeaturePython×2, Part::MultiFuse×2, Part::Cylinder×1, Part::Mirroring×1, Part::Cut×1
note: 14 computed .brp shape members not serialized (recipe doc carries the construction recipe); baked Part::Feature solids carry a one-line shape summary decoded from their .brp
EXTERNAL_REF file=Grunddaten.FCStd obj=Spreadsheet

FEATURE [Part::Box] Box  label="Cube"
  AttacherType = Attacher::AttachEngine3D
  Height = 27
  Length = 97
  Width = 400
  expr: Length = <<Grunddaten>>#Spreadsheet.Hoehe
  expr: Width = <<Grunddaten>>#Spreadsheet.Plattenbreite
  expr: Height = <<Grunddaten>>#Spreadsheet.Plattendicke
FEATURE [App::FeaturePython] Constraints  # WARN: FeaturePython — macro-defined, semantics opaque (R4)
  _Version = 1
FEATURE [Part::Cylinder] Cylinder
  Angle = 360
  AttacherType = Attacher::AttachEngine3D
  FirstAngle = 0
  Height = 30
  Placement = pos=(69.5,50,0) rot=(0,0,1;0rad)
  Radius = 17.5
  SecondAngle = 0
  expr: .Placement.Base.x = <<Grunddaten>>#Spreadsheet.Hoehe - Radius - 10mm
FEATURE [Part::Box] Box001  label="Cube001"
  AttacherType = Attacher::AttachEngine3D
  Height = 30
  Length = 35
  Placement = pos=(69.5,32.5,0) rot=(0,0,1;0rad)
  Width = 35
  expr: Length = 2 * Cylinder.Radius
  expr: Width = 2 * Cylinder.Radius
  expr: .Placement.Base.x = <<Grunddaten>>#Spreadsheet.Hoehe - Length / 2 - 10mm
  expr: .Placement.Base.y = 50mm - Width / 2
FEATURE [Part::MultiFuse] Fusion
  Shapes = -> [Cylinder,Box001]
FEATURE [Part::Mirroring] Part__Mirroring  label="Fusion (Mirror #1)"
  Base = (0,200,0)
  Normal = (0,1,0)
  Source = -> Fusion
FEATURE [Part::MultiFuse] Fusion001
  Shapes = -> [Fusion,Part__Mirroring]
FEATURE [Part::Cut] Cut
  Base = -> Box
  Tool = -> Fusion001
FEATURE [Part::FeaturePython] Parts  # WARN: FeaturePython — macro-defined, semantics opaque (R4)
  Group = -> [Box,Cylinder,Box001,Fusion,Part__Mirroring,Fusion001,Cut]
  GroupMode = 0
FEATURE [Part::FeaturePython] Assembly  label="Seitenteil"  # WARN: FeaturePython — macro-defined, semantics opaque (R4)
  AutoRelax = true
  BuildShape = 0
  Freeze = false
  Group = -> [Constraints,Elements,Parts]
  Verbose = false
  _SolverType = 1
  _Version = 1
FEATURE [App::FeaturePython] Elements  # WARN: FeaturePython — macro-defined, semantics opaque (R4)
  Group = -> [Element,Element001,Element002,Element003,Element004,Element005]
FEATURE [Part::FeaturePython] Element  label="Oben"  # link proxy (typed FeaturePython)
  Detach = false
  LinkTransform = true
  LinkedObject = -> Box [Face2]
  _Parent = -> Elements
FEATURE [Part::FeaturePython] Element001  label="Seite"  # link proxy (typed FeaturePython)
  Detach = false
  LinkTransform = true
  LinkedObject = -> Box [Face6]
  _Parent = -> Elements
FEATURE [Part::FeaturePython] Element002  label="Vorne"  # link proxy (typed FeaturePython)
  Detach = false
  LinkTransform = true
  LinkedObject = -> Box [Face3]
  _Parent = -> Elements
FEATURE [Part::FeaturePython] Element003  # link proxy (typed FeaturePython)
  Detach = false
  LinkTransform = true
  LinkedObject = -> Box [Face5]
  _Parent = -> Elements
FEATURE [Part::FeaturePython] Element004  # link proxy (typed FeaturePython)
  Detach = false
  LinkTransform = true
  LinkedObject = -> Box [Face1]
  _Parent = -> Elements
FEATURE [Part::FeaturePython] Element005  # link proxy (typed FeaturePython)
  Detach = false
  LinkTransform = true
  LinkedObject = -> Box [Face4]
  _Parent = -> Elements
---- part Zange.FCStd = doc fcstd_8ed8d12e8266 ----
FCSTD DOCUMENT  (FreeCAD 0.20R25131 (Git))
Label: Zange
License: All rights reserved
LicenseURL: http://en.wikipedia.org/wiki/All_rights_reserved
objects: Part::FeaturePython×10, Part::Cylinder×3, App::FeaturePython×2, Part::Box×1, Part::MultiFuse×1, Part::Cut×1
note: 15 computed .brp shape members not serialized (recipe doc carries the construction recipe); baked Part::Feature solids carry a one-line shape summary decoded from their .brp
EXTERNAL_REF file=Grunddaten.FCStd obj=Spreadsheet

FEATURE [Part::Box] Box  label="Cube"
  AttacherType = Attacher::AttachEngine3D
  Height = 27
  Length = 620
  Placement = pos=(-310,0,0) rot=(0,0,1;0rad)
  Width = 97
  expr: .Placement.Base.x = -Length / 2
  expr: Length = <<Grunddaten>>#Spreadsheet.Arbeitsflaeche + 2 * <<Grunddaten>>#Spreadsheet.Ueberstand
  expr: Width = <<Grunddaten>>#Spreadsheet.Hoehe
  expr: Height = <<Grunddaten>>#Spreadsheet.Plattendicke
FEATURE [Part::Cylinder] Cylinder  label="Führung_rechts"
  Angle = 360
  AttacherType = Attacher::AttachEngine3D
  FirstAngle = 0
  Height = 30
  Placement = pos=(84,40,0) rot=(0,0,1;0rad)
  Radius = 15
  SecondAngle = 0
  expr: .Placement.Base.y = -Grunddaten#Spreadsheet.Plattendicke + Grunddaten#Spreadsheet.Hoehe - Grunddaten#Spreadsheet.Spindel_Hoehe
  expr: .Placement.Base.x = Grunddaten#Spreadsheet.Spindel_Links
FEATURE [Part::Cylinder] Cylinder001  label="Führung_links"
  Angle = 360
  AttacherType = Attacher::AttachEngine3D
  FirstAngle = 0
  Height = 30
  Placement = pos=(-84,40,0) rot=(0,0,1;0rad)
  Radius = 15
  SecondAngle = 0
  expr: .Placement.Base.y = -Grunddaten#Spreadsheet.Plattendicke + Grunddaten#Spreadsheet.Hoehe - Grunddaten#Spreadsheet.Spindel_Hoehe
  expr: .Placement.Base.x = -Grunddaten#Spreadsheet.Spindel_Links
FEATURE [Part::Cylinder] Cylinder002  label="Spindel"
  Angle = 360
  AttacherType = Attacher::AttachEngine3D
  FirstAngle = 0
  Height = 30
  Placement = pos=(24,30,0) rot=(0,0,1;0rad)
  Radius = 17.5
  SecondAngle = 0
  expr: .Placement.Base.x = Grunddaten#Spreadsheet.Spindel_Antrieb
  expr: .Placement.Base.y = -Grunddaten#Spreadsheet.Plattendicke + Grunddaten#Spreadsheet.Hoehe - Grunddaten#Spreadsheet.Spindel_Antrieb_Hoehe
FEATURE [App::FeaturePython] Constraints  # WARN: FeaturePython — macro-defined, semantics opaque (R4)
  _Version = 1
FEATURE [Part::MultiFuse] Fusion
  Shapes = -> [Cylinder,Cylinder001,Cylinder002]
FEATURE [Part::Cut] Cut
  Base = -> Box
  Tool = -> Fusion
FEATURE [Part::FeaturePython] Parts  # WARN: FeaturePython — macro-defined, semantics opaque (R4)
  Group = -> [Box,Cylinder,Cylinder001,Cylinder002,Fusion,Cut]
  GroupMode = 0
FEATURE [Part::FeaturePython] Assembly  label="Zange"  # WARN: FeaturePython — macro-defined, semantics opaque (R4)
  AutoRelax = true
  BuildShape = 0
  Freeze = false
  Group = -> [Constraints,Elements,Parts]
  Verbose = false
  _SolverType = 1
  _Version = 1
FEATURE [App::FeaturePython] Elements  # WARN: FeaturePython — macro-defined, semantics opaque (R4)
  Group = -> [Element,Element001,Element002,Element003,Element004,Element005,Element006,Element007]
FEATURE [Part::FeaturePython] Element  label="Vorne"  # link proxy (typed FeaturePython)
  Detach = false
  LinkTransform = true
  LinkedObject = -> Cut [Face3]
  _Parent = -> Elements
FEATURE [Part::FeaturePython] Element001  label="Oben"  # link proxy (typed FeaturePython)
  Detach = false
  LinkTransform = true
  LinkedObject = -> Cut [Face4]
  _Parent = -> Elements
FEATURE [Part::FeaturePython] Element002  label="Spindel"  # link proxy (typed FeaturePython)
  Detach = false
  LinkTransform = true
  LinkedObject = -> Cut [Face7]
  _Parent = -> Elements
FEATURE [Part::FeaturePython] Element003  label="Hinten"  # link proxy (typed FeaturePython)
  Detach = false
  LinkTransform = true
  LinkedObject = -> Cut [Face5]
  _Parent = -> Elements
FEATURE [Part::FeaturePython] Element004  # link proxy (typed FeaturePython)
  Detach = false
  LinkTransform = true
  LinkedObject = -> Cut [Edge10]
  _Parent = -> Elements
FEATURE [Part::FeaturePython] Element005  # link proxy (typed FeaturePython)
  Detach = false
  LinkTransform = true
  LinkedObject = -> Cut [Face6]
  _Parent = -> Elements
FEATURE [Part::FeaturePython] Element006  # link proxy (typed FeaturePython)
  Detach = false
  LinkTransform = true
  LinkedObject = -> Cut [Face2]
  _Parent = -> Elements
FEATURE [Part::FeaturePython] Element007  # link proxy (typed FeaturePython)
  Detach = false
  LinkTransform = true
  LinkedObject = -> Cut [Face1]
  _Parent = -> Elements
